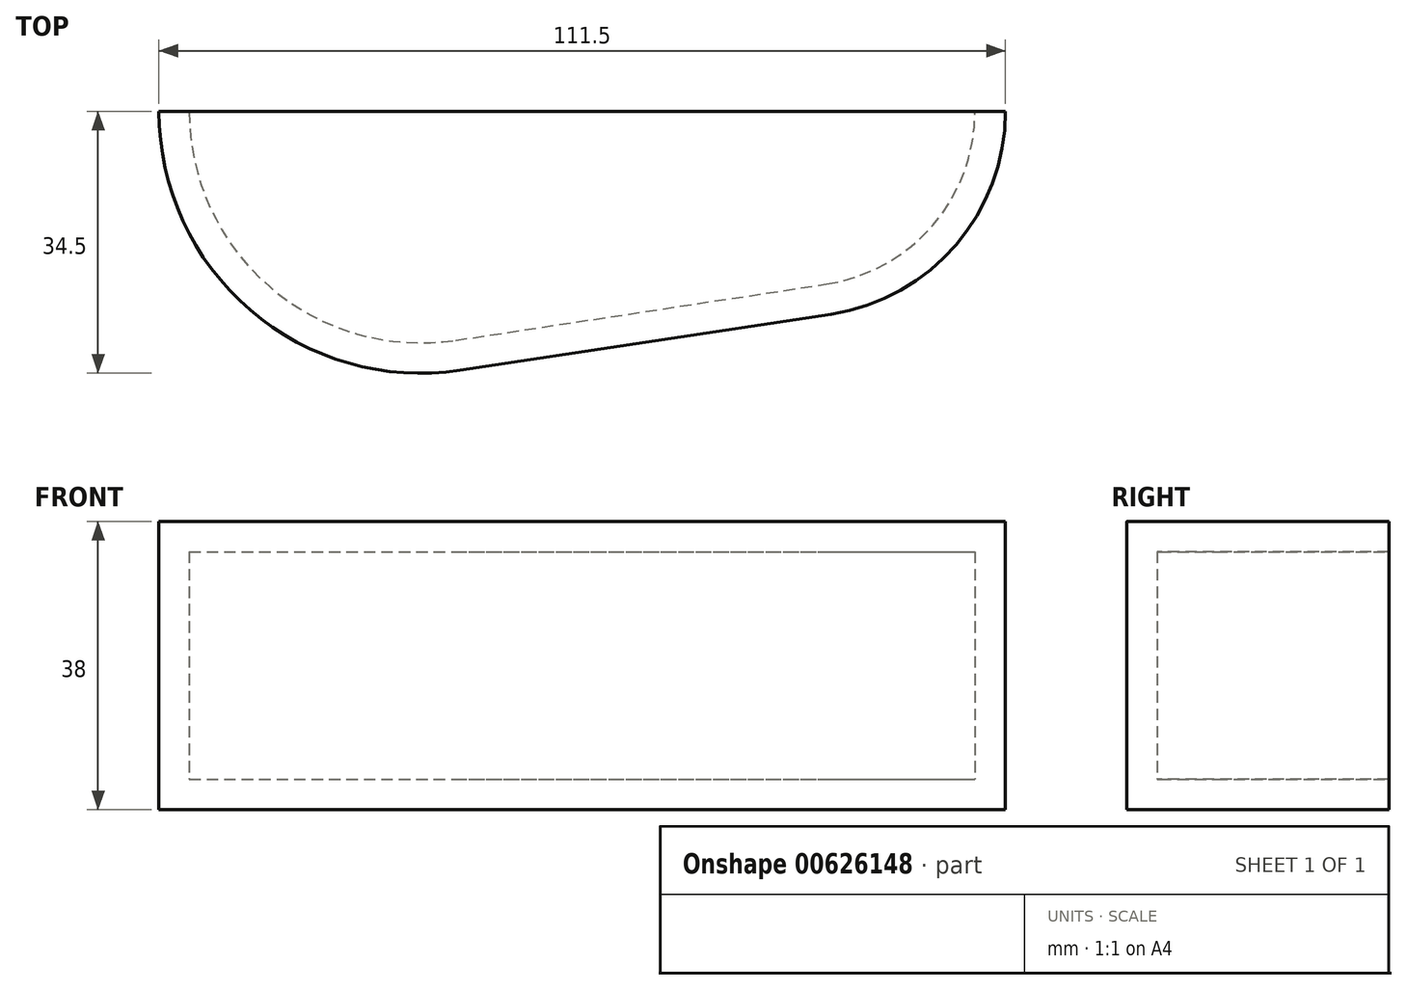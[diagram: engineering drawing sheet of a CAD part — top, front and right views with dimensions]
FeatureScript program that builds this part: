
annotation { "Feature Type Name" : "Feature", "Feature Type Description" : "" }
export const myFeature = defineFeature(function(context is Context, id is Id, definition is map)
    precondition{}
    {
        {
            var Q0;
            Q0=qCreatedBy(makeId("Top.planeOp"),FACE);
            var sketch = newSketch(context, id + "F0", { "sketchPlane" : qUnion([Q0])});
            skArc(sketch, "E0", {"start": v(-94.09, 0) * mm, "mid": v(-59.59, -34.5) * mm, "end": v(-25.09, 0) * mm});
            skArc(sketch, "E1", {"start": v(-36.59, 0) * mm, "mid": v(-9.59, -27) * mm, "end": v(17.41, 0) * mm});
            skLineSegment(sketch, "E2", {"start": v(-54.41, -34.1) * mm, "end": v(-5.54, -26.7) * mm});
            skLineSegment(sketch, "E3", {"start": v(-94.09, 0) * mm, "end": v(17.41, 0) * mm});
            skSolve(sketch);
        }
        {
            var Q0;
            Q0 = qSketchRegion(id + "F0", true);
            extrude(context, id + "F1", {"entities" : qUnion([Q0]), "endBound" : BoundingType.SYMMETRIC, "depth" : 38 * mm, "offsetDistance" : 25 * mm});
        }
        {
            var Q0;
            Q0=makeQuery(id+"F1.opExtrude","SWEPT_FACE",FACE,{"disambiguationData":[OSD([sQuery(id+"F0.wireOp",EDGE,"E3")])]});
            shell(context, id + "F2", {"entities" : qUnion([Q0]), "thickness" : 4 * mm});
        }
    });
